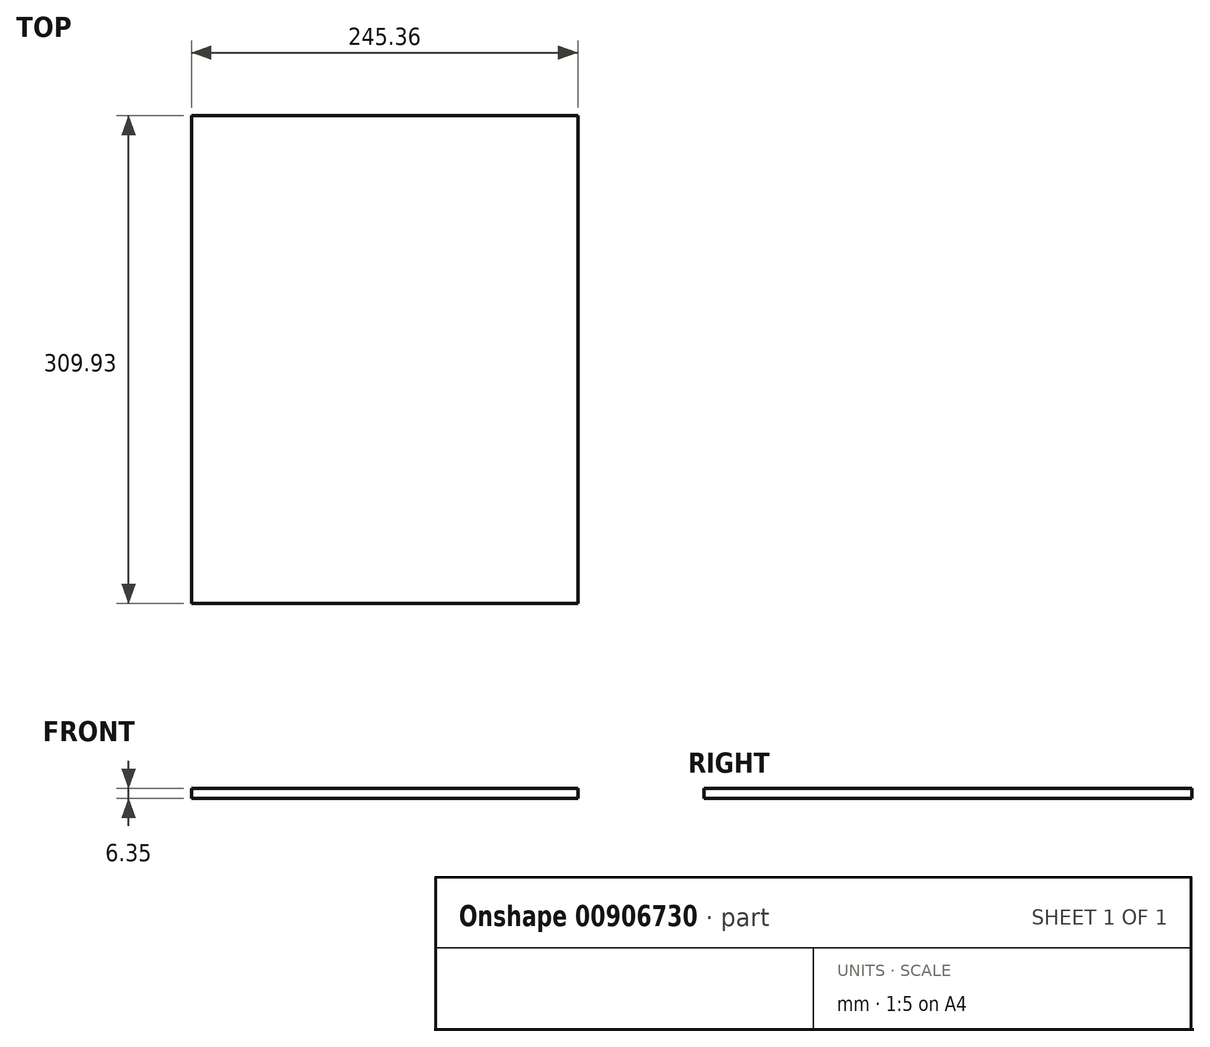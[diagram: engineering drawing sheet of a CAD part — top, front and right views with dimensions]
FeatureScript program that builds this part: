
annotation { "Feature Type Name" : "Feature", "Feature Type Description" : "" }
export const myFeature = defineFeature(function(context is Context, id is Id, definition is map)
    precondition{}
    {
        {
            var Q0;
            Q0=qCreatedBy(makeId("Top.planeOp"),FACE);
            var sketch = newSketch(context, id + "F0", { "sketchPlane" : qUnion([Q0])});
            skLineSegment(sketch, "E0.bottom", {"start": v(-121.11, 212.02) * mm, "end": v(124.25, 212.02) * mm});
            skLineSegment(sketch, "E0.top", {"start": v(-121.11, -97.9) * mm, "end": v(124.25, -97.9) * mm});
            skLineSegment(sketch, "E0.left", {"start": v(-121.11, 212.02) * mm, "end": v(-121.11, -97.9) * mm});
            skLineSegment(sketch, "E0.right", {"start": v(124.25, 212.02) * mm, "end": v(124.25, -97.9) * mm});
            skSolve(sketch);
        }
        {
            var Q0;
            Q0 = qSketchRegion(id + "F0", true);
            extrude(context, id + "F1", {"entities" : qUnion([Q0]), "depth" : 6.35 * mm, "offsetDistance" : 25.4 * mm});
        }
    });
